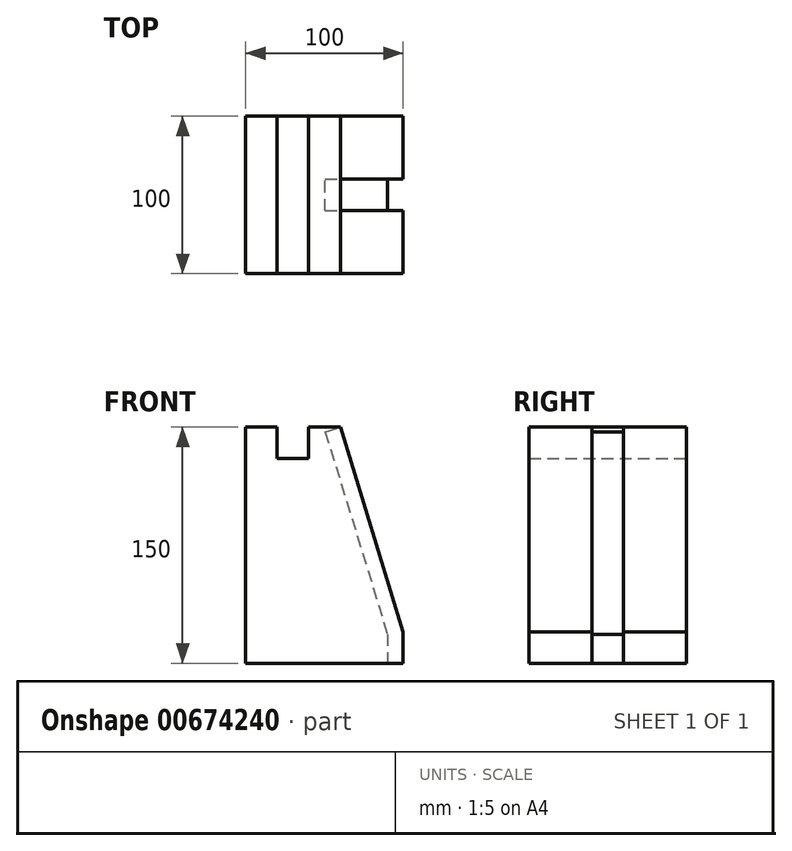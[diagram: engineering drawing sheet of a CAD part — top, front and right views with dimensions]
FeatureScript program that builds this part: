
annotation { "Feature Type Name" : "Feature", "Feature Type Description" : "" }
export const myFeature = defineFeature(function(context is Context, id is Id, definition is map)
    precondition{}
    {
        {
            var Q0;
            Q0=qCreatedBy(makeId("Front.planeOp"),FACE);
            var sketch = newSketch(context, id + "F0", { "sketchPlane" : qUnion([Q0])});
            skLineSegment(sketch, "E0", {"start": v(0, 0) * mm, "end": v(0, 150) * mm});
            skLineSegment(sketch, "E1", {"start": v(0, 150) * mm, "end": v(0, 0) * mm});
            skLineSegment(sketch, "E2", {"start": v(100, 0) * mm, "end": v(0, 0) * mm});
            skLineSegment(sketch, "E3", {"start": v(100, 0) * mm, "end": v(100, 20) * mm});
            skLineSegment(sketch, "E4", {"start": v(0, 150) * mm, "end": v(20, 150) * mm});
            skLineSegment(sketch, "E5", {"start": v(20, 130) * mm, "end": v(20, 150) * mm});
            skLineSegment(sketch, "E6", {"start": v(20, 130) * mm, "end": v(40, 130) * mm});
            skLineSegment(sketch, "E7", {"start": v(40, 150) * mm, "end": v(40, 130) * mm});
            skLineSegment(sketch, "E8", {"start": v(40, 150) * mm, "end": v(60.05, 150) * mm});
            skLineSegment(sketch, "E9", {"start": v(60.05, 150) * mm, "end": v(100, 20) * mm});
            skSolve(sketch);
        }
        {
            var Q0;
            Q0 = qSketchRegion(id + "F0", true);
            extrude(context, id + "F1", {"entities" : qUnion([Q0]), "depth" : 100 * mm, "offsetDistance" : 25 * mm});
        }
        {
            var Q0;
            Q0=makeQuery(id+"F1.opExtrude","SWEPT_FACE",FACE,{"disambiguationData":[OSD([sQuery(id+"F0.wireOp",EDGE,"E9")])]});
            var sketch = newSketch(context, id + "F2", { "sketchPlane" : qUnion([Q0])});
            skLineSegment(sketch, "E10", {"start": v(-100, 125.74) * mm, "end": v(-60, 125.74) * mm});
            skLineSegment(sketch, "E11", {"start": v(-60, 125.74) * mm, "end": v(-40, 125.74) * mm});
            skLineSegment(sketch, "E12", {"start": v(-40, 125.74) * mm, "end": v(0, 125.74) * mm});
            skLineSegment(sketch, "E13", {"start": v(-71.73, 125.74) * mm, "end": v(-76.32, 125.74) * mm});
            skLineSegment(sketch, "E14", {"start": v(-76.32, 125.74) * mm, "end": v(-27.1, 125.74) * mm});
            skLineSegment(sketch, "E15", {"start": v(-60, 125.74) * mm, "end": v(-60, -10.26) * mm});
            skLineSegment(sketch, "E16", {"start": v(-40, 125.74) * mm, "end": v(-40, -10.26) * mm});
            skPoint(sketch, "E16.endSnap0", {"position": v(-50, -10.26) * mm});
            skSolve(sketch);
        }
        {
            var Q0;
            Q0=makeQuery(id+"F1.opExtrude","SWEPT_FACE",FACE,{"disambiguationData":[OSD([sQuery(id+"F0.wireOp",EDGE,"E3")])]});
            var sketch = newSketch(context, id + "F3", { "sketchPlane" : qUnion([Q0])});
            skLineSegment(sketch, "E17", {"start": v(-100, 20) * mm, "end": v(-60, 20) * mm});
            skLineSegment(sketch, "E18", {"start": v(-60, 20) * mm, "end": v(-40, 20) * mm});
            skLineSegment(sketch, "E19", {"start": v(-40, 20) * mm, "end": v(0, 20) * mm});
            skLineSegment(sketch, "E20", {"start": v(-60, 20) * mm, "end": v(-60, 0) * mm});
            skLineSegment(sketch, "E21", {"start": v(-40, 20) * mm, "end": v(-40, 0) * mm});
            skSolve(sketch);
        }
        {
            var Q0;
            Q0=makeQuery(id+"F3.imprint","IMPRINT",FACE,{"disambiguationData":[TD([[makeQuery(id+"F3.imprint","IMPRINT",EDGE,{"derivedFrom":sQuery(id+"F3.wireOp",EDGE,"E18")}),-1.0]])]});
            extrude(context, id + "F4", {"entities" : qUnion([Q0]), "operationType" : NewBodyOperationType.REMOVE, "oppositeDirection" : true, "depth" : 10 * mm, "offsetDistance" : 25 * mm});
        }
        {
            var Q0;
            {var subQ0=sQuery(id+"F2.wireOp",EDGE,"E15");Q0=makeQuery(id+"F2.imprint","IMPRINT",FACE,{"disambiguationData":[TD([[makeQuery(id+"F2.imprint","IMPRINT",EDGE,{"derivedFrom":subQ0}),1.0]])]});}
            extrude(context, id + "F5", {"entities" : qUnion([Q0]), "operationType" : NewBodyOperationType.ADD, "depth" : 10 * mm, "offsetDistance" : 25 * mm});
        }
        {
            var Q0;
            Q0=makeQuery(id+"F5.opExtrude","CAP_FACE",FACE,{"disambiguationData":[OSD([sQuery(id+"F0.wireOp",EDGE,"E3"),sQuery(id+"F0.wireOp",EDGE,"E9"),sQuery(id+"F2.wireOp",EDGE,"E14"),sQuery(id+"F2.wireOp",EDGE,"E15"),sQuery(id+"F2.wireOp",EDGE,"E16")])],"isStart":false});
            extrude(context, id + "F6", {"entities" : qUnion([Q0]), "operationType" : NewBodyOperationType.REMOVE, "oppositeDirection" : true, "depth" : 10 * mm, "offsetDistance" : 25 * mm});
        }
        {
            var Q0;
            {var subQ0=sQuery(id+"F2.wireOp",EDGE,"E16");var subQ1=sQuery(id+"F2.wireOp",EDGE,"E15");var subQ2=sQuery(id+"F2.wireOp",EDGE,"E14");var subQ3=sQuery(id+"F0.wireOp",EDGE,"E9");var subQ4=sQuery(id+"F0.wireOp",EDGE,"E3");var subQ17=makeQuery(id+"F1.opExtrude","SWEPT_FACE",FACE,{"disambiguationData":[OSD([subQ3])]});Q0=makeQuery(id+"F6.boolean.opBoolean","MERGE",FACE,{"derivedFrom":[makeQuery(id+"F5.boolean.opBoolean","SPLIT",FACE,{"disambiguationData":[TD([makeQuery(id+"F4.boolean.opBoolean","COPY",FACE,{"derivedFrom":makeQuery(id+"F4.opExtrude","SWEPT_FACE",FACE,{"disambiguationData":[OSD([sQuery(id+"F3.wireOp",EDGE,"E21")])]})})])],"derivedFrom":subQ17}),makeQuery(id+"F5.boolean.opBoolean","SPLIT",FACE,{"disambiguationData":[TD([makeQuery(id+"F4.boolean.opBoolean","COPY",FACE,{"derivedFrom":makeQuery(id+"F4.opExtrude","SWEPT_FACE",FACE,{"disambiguationData":[OSD([sQuery(id+"F3.wireOp",EDGE,"E20")])]})})])],"derivedFrom":subQ17}),makeQuery(id+"F6.opExtrude","CAP_FACE",FACE,{"disambiguationData":[OSD([subQ4,subQ3,subQ2,subQ1,subQ0])],"isStart":false})]});}
            var sketch = newSketch(context, id + "F7", { "sketchPlane" : qUnion([Q0])});
            skLineSegment(sketch, "E22", {"start": v(-100, 125.74) * mm, "end": v(-60, 125.74) * mm});
            skLineSegment(sketch, "E23", {"start": v(-60, 125.74) * mm, "end": v(-40, 125.74) * mm});
            skLineSegment(sketch, "E24", {"start": v(-40, 125.74) * mm, "end": v(0, 125.74) * mm});
            skLineSegment(sketch, "E25", {"start": v(-60, 125.74) * mm, "end": v(-60, -10.26) * mm});
            skLineSegment(sketch, "E26", {"start": v(-40, 125.74) * mm, "end": v(-40, -10.26) * mm});
            skSolve(sketch);
        }
        {
            var Q0;
            Q0=makeQuery(id+"F7.imprint","IMPRINT",FACE,{"disambiguationData":[TD([[makeQuery(id+"F7.imprint","IMPRINT",EDGE,{"derivedFrom":sQuery(id+"F7.wireOp",EDGE,"E23")}),-1.0]])]});
            extrude(context, id + "F8", {"entities" : qUnion([Q0]), "operationType" : NewBodyOperationType.REMOVE, "oppositeDirection" : true, "depth" : 10 * mm, "offsetDistance" : 25 * mm});
        }
    });
